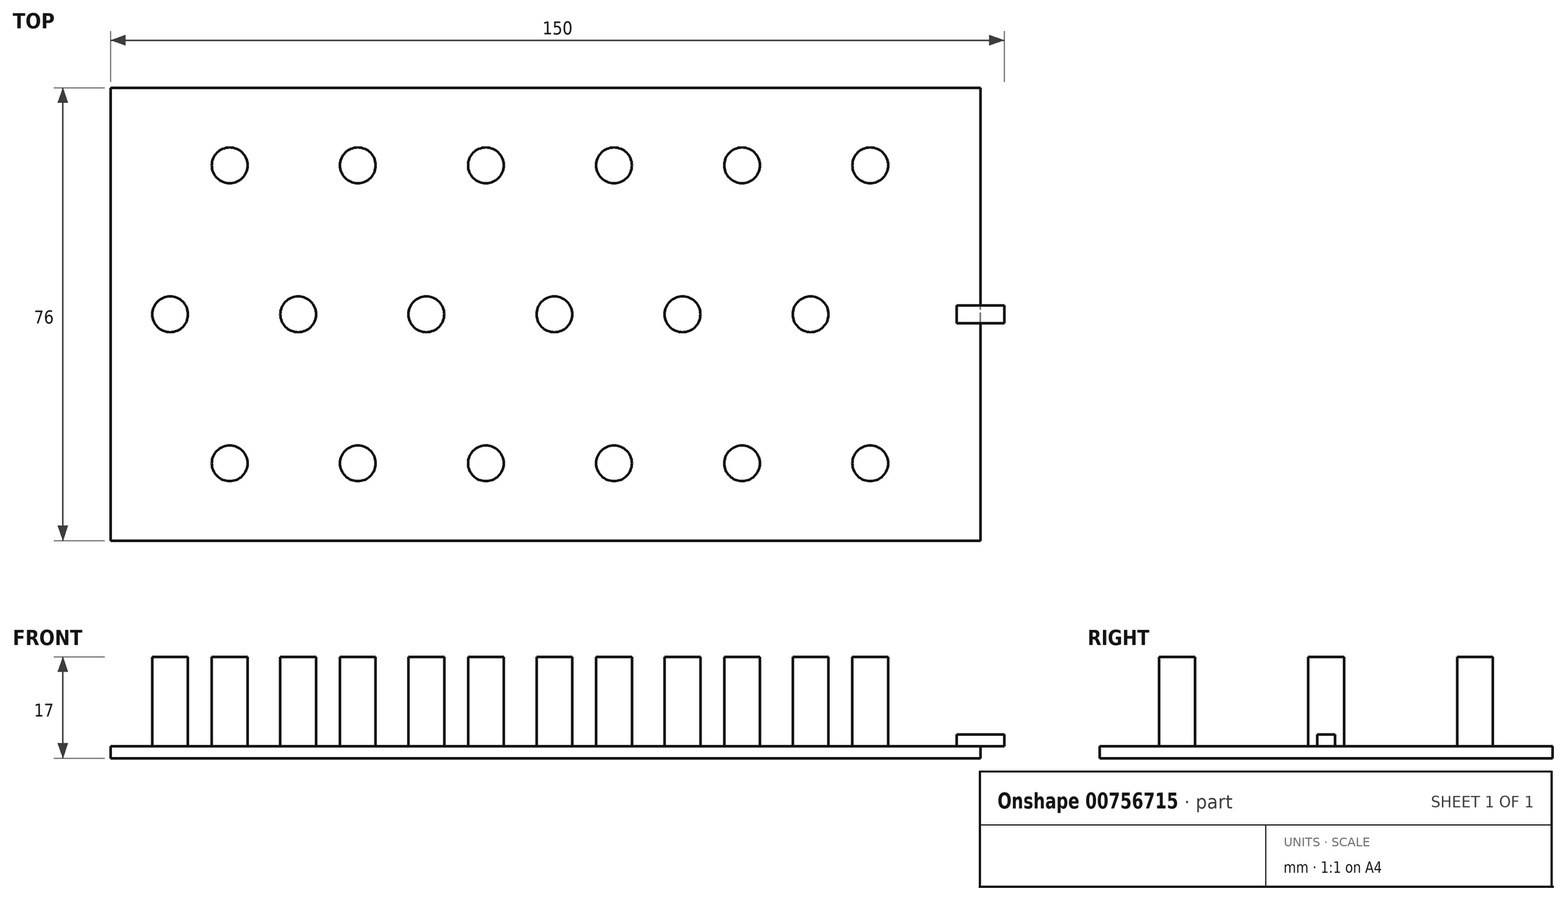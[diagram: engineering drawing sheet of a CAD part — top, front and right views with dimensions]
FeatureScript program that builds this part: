
annotation { "Feature Type Name" : "Feature", "Feature Type Description" : "" }
export const myFeature = defineFeature(function(context is Context, id is Id, definition is map)
    precondition{}
    {
        {
            var Q0;
            Q0=qCreatedBy(makeId("Top.planeOp"),FACE);
            var sketch = newSketch(context, id + "F0", { "sketchPlane" : qUnion([Q0])});
            skLineSegment(sketch, "E0.bottom", {"start": v(73, -38) * mm, "end": v(-73, -38) * mm});
            skLineSegment(sketch, "E0.top", {"start": v(73, 38) * mm, "end": v(-73, 38) * mm});
            skLineSegment(sketch, "E0.left", {"start": v(73, -38) * mm, "end": v(73, 38) * mm});
            skLineSegment(sketch, "E0.right", {"start": v(-73, -38) * mm, "end": v(-73, 38) * mm});
            skPoint(sketch, "E0.middle", {"position": v(0, 0) * mm});
            skSolve(sketch);
        }
        {
            var Q0;
            Q0=makeQuery(id+"F0.imprint","IMPRINT",FACE,{"disambiguationData":[TD([[makeQuery(id+"F0.imprint","IMPRINT",EDGE,{"derivedFrom":sQuery(id+"F0.wireOp",EDGE,"E0.bottom")}),-1.0]])]});
            extrude(context, id + "F1", {"entities" : qUnion([Q0]), "depth" : 2 * mm, "offsetDistance" : 25 * mm});
        }
        {
            var Q0;
            Q0=makeQuery(id+"F1.opExtrude","CAP_FACE",FACE,{"disambiguationData":[OSD([sQuery(id+"F0.wireOp",EDGE,"E0.bottom"),sQuery(id+"F0.wireOp",EDGE,"E0.top"),sQuery(id+"F0.wireOp",EDGE,"E0.left"),sQuery(id+"F0.wireOp",EDGE,"E0.right")])],"isStart":false});
            var sketch = newSketch(context, id + "F2", { "sketchPlane" : qUnion([Q0])});
            skLineSegment(sketch, "E1.bottom", {"start": v(77, -1.5) * mm, "end": v(69, -1.5) * mm});
            skLineSegment(sketch, "E1.top", {"start": v(77, 1.5) * mm, "end": v(69, 1.5) * mm});
            skLineSegment(sketch, "E1.left", {"start": v(77, -1.5) * mm, "end": v(77, 1.5) * mm});
            skLineSegment(sketch, "E1.right", {"start": v(69, -1.5) * mm, "end": v(69, 1.5) * mm});
            skPoint(sketch, "E1.middle", {"position": v(73, 0) * mm});
            skCircle(sketch, "E2", {"center": v(-53, 25) * mm, "radius": 3 * mm});
            skLineSegment(sketch, "E3", {"start": v(-73, 25) * mm, "end": v(73, 25) * mm, "construction": true});
            skCircle(sketch, "E4.1.0.0", {"center": v(-31.5, 25) * mm, "radius": 3 * mm});
            skCircle(sketch, "E4.2.0.0", {"center": v(-10, 25) * mm, "radius": 3 * mm});
            skCircle(sketch, "E4.3.0.0", {"center": v(11.5, 25) * mm, "radius": 3 * mm});
            skCircle(sketch, "E4.4.0.0", {"center": v(33, 25) * mm, "radius": 3 * mm});
            skLineSegment(sketch, "E4.direction1", {"start": v(-53, 25) * mm, "end": v(-31.5, 25) * mm, "construction": true});
            skLineSegment(sketch, "E5", {"start": v(-73, 0) * mm, "end": v(73, 0) * mm, "construction": true});
            skCircle(sketch, "E6", {"center": v(-63, 0) * mm, "radius": 3 * mm});
            skCircle(sketch, "E7.1.0.0", {"center": v(-41.5, 0) * mm, "radius": 3 * mm});
            skCircle(sketch, "E7.2.0.0", {"center": v(-20, 0) * mm, "radius": 3 * mm});
            skCircle(sketch, "E7.3.0.0", {"center": v(1.5, 0) * mm, "radius": 3 * mm});
            skCircle(sketch, "E7.4.0.0", {"center": v(23, 0) * mm, "radius": 3 * mm});
            skCircle(sketch, "E7.5.0.0", {"center": v(44.5, 0) * mm, "radius": 3 * mm});
            skLineSegment(sketch, "E7.direction1", {"start": v(-63, 0) * mm, "end": v(-41.5, 0) * mm, "construction": true});
            skCircle(sketch, "E8.0.5.0", {"center": v(54.5, 25) * mm, "radius": 3 * mm});
            skCircle(sketch, "E9.0.1.0", {"center": v(-53, -25) * mm, "radius": 3 * mm});
            skCircle(sketch, "E9.0.1.1", {"center": v(-31.5, -25) * mm, "radius": 3 * mm});
            skCircle(sketch, "E9.0.1.2", {"center": v(-10, -25) * mm, "radius": 3 * mm});
            skCircle(sketch, "E9.0.1.3", {"center": v(11.5, -25) * mm, "radius": 3 * mm});
            skCircle(sketch, "E9.0.1.4", {"center": v(33, -25) * mm, "radius": 3 * mm});
            skCircle(sketch, "E9.0.1.5", {"center": v(54.5, -25) * mm, "radius": 3 * mm});
            skLineSegment(sketch, "E9.direction1", {"start": v(-53, 25) * mm, "end": v(-26.7, 25) * mm, "construction": true});
            skLineSegment(sketch, "E9.direction2", {"start": v(-53, 25) * mm, "end": v(-53, -25) * mm, "construction": true});
            skSolve(sketch);
        }
        {
            var Q0;
            Q0=makeQuery(id+"F2.imprint","IMPRINT",FACE,{"disambiguationData":[TD([[makeQuery(id+"F2.imprint","IMPRINT",EDGE,{"derivedFrom":sQuery(id+"F2.wireOp",EDGE,"E2")}),1.0]])]});
            var Q1;
            Q1=makeQuery(id+"F2.imprint","IMPRINT",FACE,{"disambiguationData":[TD([[makeQuery(id+"F2.imprint","IMPRINT",EDGE,{"derivedFrom":sQuery(id+"F2.wireOp",EDGE,"E4.1.0.0")}),1.0]])]});
            var Q2;
            Q2=makeQuery(id+"F2.imprint","IMPRINT",FACE,{"disambiguationData":[TD([[makeQuery(id+"F2.imprint","IMPRINT",EDGE,{"derivedFrom":sQuery(id+"F2.wireOp",EDGE,"E4.2.0.0")}),1.0]])]});
            var Q3;
            Q3=makeQuery(id+"F2.imprint","IMPRINT",FACE,{"disambiguationData":[TD([[makeQuery(id+"F2.imprint","IMPRINT",EDGE,{"derivedFrom":sQuery(id+"F2.wireOp",EDGE,"E4.3.0.0")}),1.0]])]});
            var Q4;
            Q4=makeQuery(id+"F2.imprint","IMPRINT",FACE,{"disambiguationData":[TD([[makeQuery(id+"F2.imprint","IMPRINT",EDGE,{"derivedFrom":sQuery(id+"F2.wireOp",EDGE,"E4.4.0.0")}),1.0]])]});
            var Q5;
            Q5=makeQuery(id+"F2.imprint","IMPRINT",FACE,{"disambiguationData":[TD([[makeQuery(id+"F2.imprint","IMPRINT",EDGE,{"derivedFrom":sQuery(id+"F2.wireOp",EDGE,"E8.0.5.0")}),1.0]])]});
            var Q6;
            Q6=makeQuery(id+"F2.imprint","IMPRINT",FACE,{"disambiguationData":[TD([[makeQuery(id+"F2.imprint","IMPRINT",EDGE,{"derivedFrom":sQuery(id+"F2.wireOp",EDGE,"E9.0.1.5")}),1.0]])]});
            var Q7;
            Q7=makeQuery(id+"F2.imprint","IMPRINT",FACE,{"disambiguationData":[TD([[makeQuery(id+"F2.imprint","IMPRINT",EDGE,{"derivedFrom":sQuery(id+"F2.wireOp",EDGE,"E9.0.1.4")}),1.0]])]});
            var Q8;
            Q8=makeQuery(id+"F2.imprint","IMPRINT",FACE,{"disambiguationData":[TD([[makeQuery(id+"F2.imprint","IMPRINT",EDGE,{"derivedFrom":sQuery(id+"F2.wireOp",EDGE,"E9.0.1.3")}),1.0]])]});
            var Q9;
            Q9=makeQuery(id+"F2.imprint","IMPRINT",FACE,{"disambiguationData":[TD([[makeQuery(id+"F2.imprint","IMPRINT",EDGE,{"derivedFrom":sQuery(id+"F2.wireOp",EDGE,"E9.0.1.2")}),1.0]])]});
            var Q10;
            Q10=makeQuery(id+"F2.imprint","IMPRINT",FACE,{"disambiguationData":[TD([[makeQuery(id+"F2.imprint","IMPRINT",EDGE,{"derivedFrom":sQuery(id+"F2.wireOp",EDGE,"E9.0.1.1")}),1.0]])]});
            var Q11;
            Q11=makeQuery(id+"F2.imprint","IMPRINT",FACE,{"disambiguationData":[TD([[makeQuery(id+"F2.imprint","IMPRINT",EDGE,{"derivedFrom":sQuery(id+"F2.wireOp",EDGE,"E9.0.1.0")}),1.0]])]});
            var Q12;
            Q12=sQuery(id+"F2.wireOp",EDGE,"E2");
            var Q13;
            Q13=sQuery(id+"F2.wireOp",EDGE,"E4.1.0.0");
            var Q14;
            Q14=sQuery(id+"F2.wireOp",EDGE,"E4.2.0.0");
            var Q15;
            Q15=sQuery(id+"F2.wireOp",EDGE,"E4.3.0.0");
            var Q16;
            Q16=sQuery(id+"F2.wireOp",EDGE,"E4.4.0.0");
            var Q17;
            Q17=sQuery(id+"F2.wireOp",EDGE,"E8.0.5.0");
            var Q18;
            Q18=sQuery(id+"F2.wireOp",EDGE,"E9.0.1.0");
            var Q19;
            Q19=sQuery(id+"F2.wireOp",EDGE,"E9.0.1.1");
            var Q20;
            Q20=sQuery(id+"F2.wireOp",EDGE,"E9.0.1.2");
            var Q21;
            Q21=sQuery(id+"F2.wireOp",EDGE,"E9.0.1.3");
            var Q22;
            Q22=sQuery(id+"F2.wireOp",EDGE,"E9.0.1.4");
            var Q23;
            Q23=sQuery(id+"F2.wireOp",EDGE,"E9.0.1.5");
            extrude(context, id + "F3", {"entities" : qUnion([Q0, Q1, Q2, Q3, Q4, Q5, Q6, Q7, Q8, Q9, Q10, Q11]), "surfaceEntities" : qUnion([Q12, Q13, Q14, Q15, Q16, Q17, Q18, Q19, Q20, Q21, Q22, Q23]), "depth" : 15 * mm, "offsetDistance" : 25 * mm});
        }
        {
            var Q0;
            Q0=makeQuery(id+"F2.imprint","IMPRINT",FACE,{"disambiguationData":[TD([[makeQuery(id+"F2.imprint","IMPRINT",EDGE,{"derivedFrom":sQuery(id+"F2.wireOp",EDGE,"E6")}),1.0]])]});
            var Q1;
            Q1=makeQuery(id+"F2.imprint","IMPRINT",FACE,{"disambiguationData":[TD([[makeQuery(id+"F2.imprint","IMPRINT",EDGE,{"derivedFrom":sQuery(id+"F2.wireOp",EDGE,"E7.1.0.0")}),1.0]])]});
            var Q2;
            Q2=makeQuery(id+"F2.imprint","IMPRINT",FACE,{"disambiguationData":[TD([[makeQuery(id+"F2.imprint","IMPRINT",EDGE,{"derivedFrom":sQuery(id+"F2.wireOp",EDGE,"E7.2.0.0")}),1.0]])]});
            var Q3;
            Q3=makeQuery(id+"F2.imprint","IMPRINT",FACE,{"disambiguationData":[TD([[makeQuery(id+"F2.imprint","IMPRINT",EDGE,{"derivedFrom":sQuery(id+"F2.wireOp",EDGE,"E7.3.0.0")}),1.0]])]});
            var Q4;
            Q4=makeQuery(id+"F2.imprint","IMPRINT",FACE,{"disambiguationData":[TD([[makeQuery(id+"F2.imprint","IMPRINT",EDGE,{"derivedFrom":sQuery(id+"F2.wireOp",EDGE,"E7.4.0.0")}),1.0]])]});
            var Q5;
            Q5=makeQuery(id+"F2.imprint","IMPRINT",FACE,{"disambiguationData":[TD([[makeQuery(id+"F2.imprint","IMPRINT",EDGE,{"derivedFrom":sQuery(id+"F2.wireOp",EDGE,"E7.5.0.0")}),1.0]])]});
            var Q6;
            Q6=sQuery(id+"F2.wireOp",EDGE,"E6");
            var Q7;
            Q7=sQuery(id+"F2.wireOp",EDGE,"E7.1.0.0");
            var Q8;
            Q8=sQuery(id+"F2.wireOp",EDGE,"E7.2.0.0");
            var Q9;
            Q9=sQuery(id+"F2.wireOp",EDGE,"E7.3.0.0");
            var Q10;
            Q10=sQuery(id+"F2.wireOp",EDGE,"E7.4.0.0");
            var Q11;
            Q11=sQuery(id+"F2.wireOp",EDGE,"E7.5.0.0");
            extrude(context, id + "F4", {"entities" : qUnion([Q0, Q1, Q2, Q3, Q4, Q5]), "surfaceEntities" : qUnion([Q6, Q7, Q8, Q9, Q10, Q11]), "depth" : 15 * mm, "offsetDistance" : 25 * mm});
        }
        {
            var Q0;
            {var subQ0=sQuery(id+"F2.wireOp",EDGE,"E1.left");Q0=makeQuery(id+"F2.imprint","IMPRINT",FACE,{"disambiguationData":[TD([[makeQuery(id+"F2.imprint","IMPRINT",EDGE,{"derivedFrom":subQ0}),1.0]])]});}
            var Q1;
            {var subQ0=sQuery(id+"F2.wireOp",EDGE,"E1.right");Q1=makeQuery(id+"F2.imprint","IMPRINT",FACE,{"disambiguationData":[TD([[makeQuery(id+"F2.imprint","IMPRINT",EDGE,{"derivedFrom":subQ0}),-1.0]])]});}
            extrude(context, id + "F5", {"entities" : qUnion([Q0, Q1]), "operationType" : NewBodyOperationType.ADD, "depth" : 2 * mm, "offsetDistance" : 25 * mm});
        }
    });
